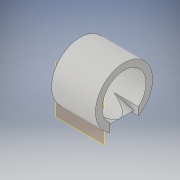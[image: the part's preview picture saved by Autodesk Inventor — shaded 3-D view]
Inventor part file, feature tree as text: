
AUTODESK INVENTOR PART (.ipt)
format: ipt  version: 2019 (Build 230136000, 136)  size: 128,512 bytes
history: native  units: in
note: dims shown in document units (in); Inventor stores cm internally (conversion verified against a paired STEP export)
features: sketch x2, plane x1, revolve x1, extrude x1
ambient origin geometry x8: Origin, YZ Plane, XZ Plane, XY Plane, X Axis, Y Axis, Z Axis, Center Point
bodies: Solid1 (feature_tree)
feature tree (5):
  plane  "Work Plane1"
  revolve  "Revolution1"  [1 undecoded]
  extrude  "Extrusion2"  TaperAngle=90.0deg  [1 undecoded]
  sketch  "Sketch2"  dims[d11=0.7874in d12=0.1181in]
  sketch  "Sketch3"  dims[d13=0.3937in d15=90.0deg d17=0.6693in d19=15.0deg d20=15.0deg d21=0.1181in d23=0.7087in d24=0.2165in d25=0.2091in d26=0.2285in d27=0.5118in d28=0.0in]
note: 2 required parameter values undecoded (feature->parameter linkage not recoverable at this tier; creation-order binding heuristic only, values carry confidence <= 0.55)